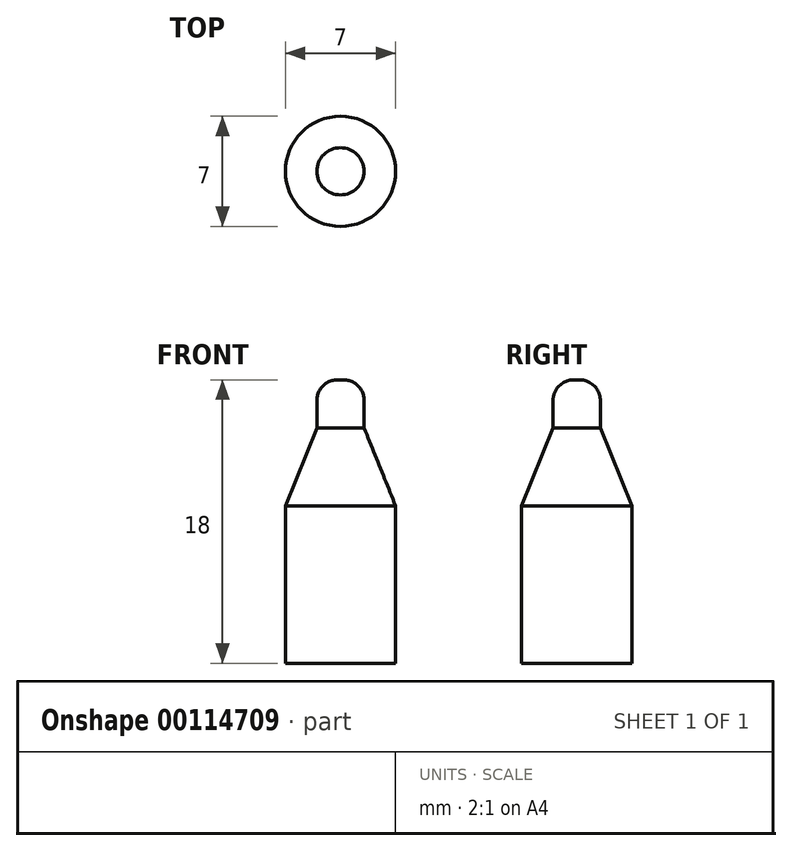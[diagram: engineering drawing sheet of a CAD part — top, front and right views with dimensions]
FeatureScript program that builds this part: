
annotation { "Feature Type Name" : "Feature", "Feature Type Description" : "" }
export const myFeature = defineFeature(function(context is Context, id is Id, definition is map)
    precondition{}
    {
        {
            var Q0;
            Q0=qCreatedBy(makeId("Top.planeOp"),FACE);
            var sketch = newSketch(context, id + "F0", { "sketchPlane" : qUnion([Q0])});
            skCircle(sketch, "E0", {"center": v(0, 0) * mm, "radius": 3.5 * mm});
            skCircle(sketch, "E1", {"center": v(0, 0) * mm, "radius": 1.5 * mm});
            skSolve(sketch);
        }
        {
            var Q0;
            Q0=makeQuery(id+"F0.imprint","IMPRINT",FACE,{"disambiguationData":[TD([[makeQuery(id+"F0.imprint","IMPRINT",EDGE,{"derivedFrom":sQuery(id+"F0.wireOp",EDGE,"E0")}),1.0]])]});
            var Q1;
            Q1=makeQuery(id+"F0.imprint","IMPRINT",FACE,{"disambiguationData":[TD([[makeQuery(id+"F0.imprint","IMPRINT",EDGE,{"derivedFrom":sQuery(id+"F0.wireOp",EDGE,"E1")}),1.0]])]});
            extrude(context, id + "F1", {"entities" : qUnion([Q0, Q1]), "depth" : 10 * mm});
        }
        {
            var Q0;
            Q0=makeQuery(id+"F1.opExtrude","CAP_FACE",FACE,{"disambiguationData":[OSD([sQuery(id+"F0.wireOp",EDGE,"E0")])],"isStart":false});
            extrude(context, id + "F2", {"entities" : qUnion([Q0]), "operationType" : NewBodyOperationType.ADD, "depth" : 5 * mm, "hasDraft" : true, "draftAngle" : 22 * degree, "draftPullDirection" : true});
        }
        {
            var Q0;
            Q0=makeQuery(id+"F0.imprint","IMPRINT",FACE,{"disambiguationData":[TD([[makeQuery(id+"F0.imprint","IMPRINT",EDGE,{"derivedFrom":sQuery(id+"F0.wireOp",EDGE,"E1")}),1.0]])]});
            var Q1;
            Q1=sQuery(id+"F0.wireOp",EDGE,"E1");
            extrude(context, id + "F3", {"entities" : qUnion([Q0]), "operationType" : NewBodyOperationType.ADD, "surfaceEntities" : qUnion([Q1]), "depth" : 18 * mm});
        }
        {
            var Q0;
            Q0=makeQuery(id+"F3.opExtrude","CAP_EDGE",EDGE,{"disambiguationData":[OSD([sQuery(id+"F0.wireOp",EDGE,"E1")])],"isStart":false});
            fillet(context, id + "F4", {"entities" : qUnion([Q0]), "radius" : 1.3 * mm, "tangentPropagation" : true, "allowEdgeOverflow" : false});
        }
    });
